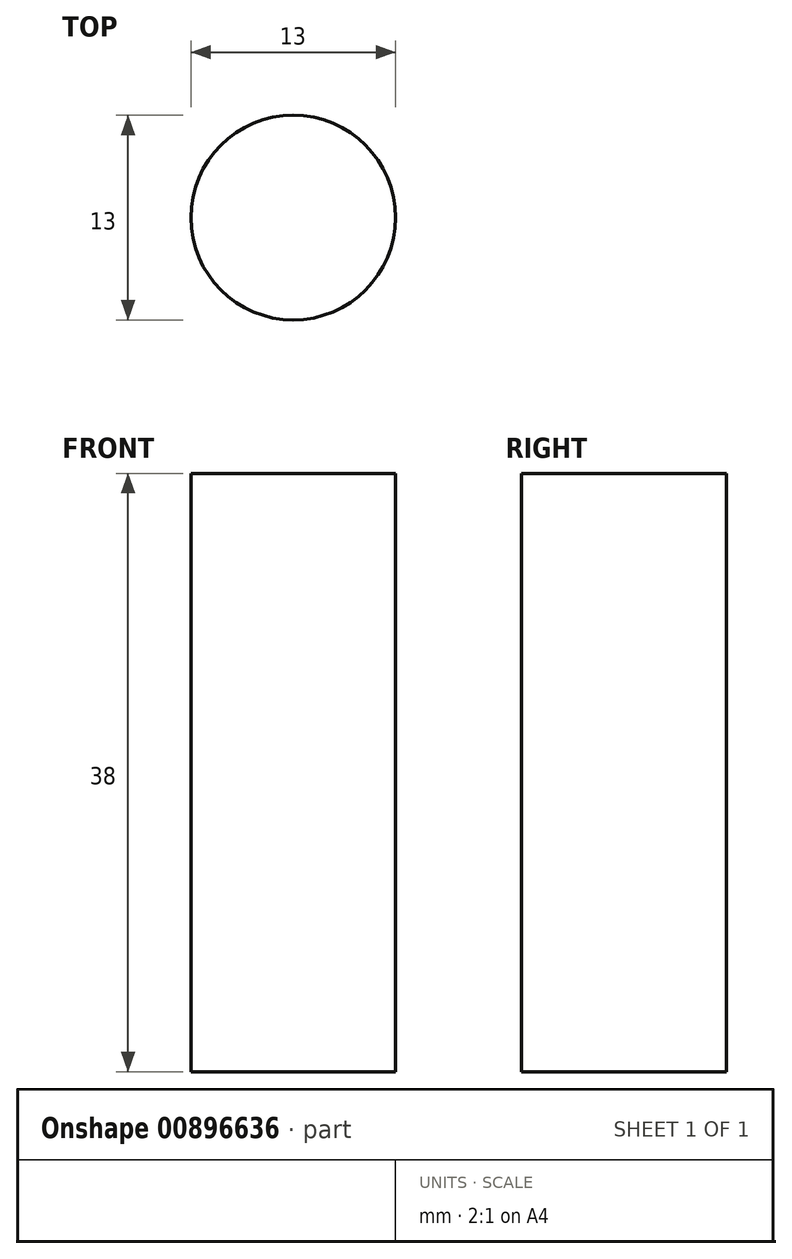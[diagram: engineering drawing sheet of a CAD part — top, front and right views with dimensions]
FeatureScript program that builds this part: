
annotation { "Feature Type Name" : "Feature", "Feature Type Description" : "" }
export const myFeature = defineFeature(function(context is Context, id is Id, definition is map)
    precondition{}
    {
        {
            var Q0;
            Q0=qCreatedBy(makeId("Top.planeOp"),FACE);
            var sketch = newSketch(context, id + "F0", { "sketchPlane" : qUnion([Q0])});
            skCircle(sketch, "E0", {"center": v(0, 0) * mm, "radius": 6.5 * mm});
            skSolve(sketch);
        }
        {
            var Q0;
            Q0=makeQuery(id+"F0.imprint","IMPRINT",FACE,{"disambiguationData":[TD([[makeQuery(id+"F0.imprint","IMPRINT",EDGE,{"derivedFrom":sQuery(id+"F0.wireOp",EDGE,"E0")}),1.0]])]});
            var Q1;
            Q1=sQuery(id+"F0.wireOp",EDGE,"E0");
            extrude(context, id + "F1", {"entities" : qUnion([Q0]), "surfaceEntities" : qUnion([Q1]), "depth" : 38 * mm, "offsetDistance" : 25 * mm});
        }
    });
